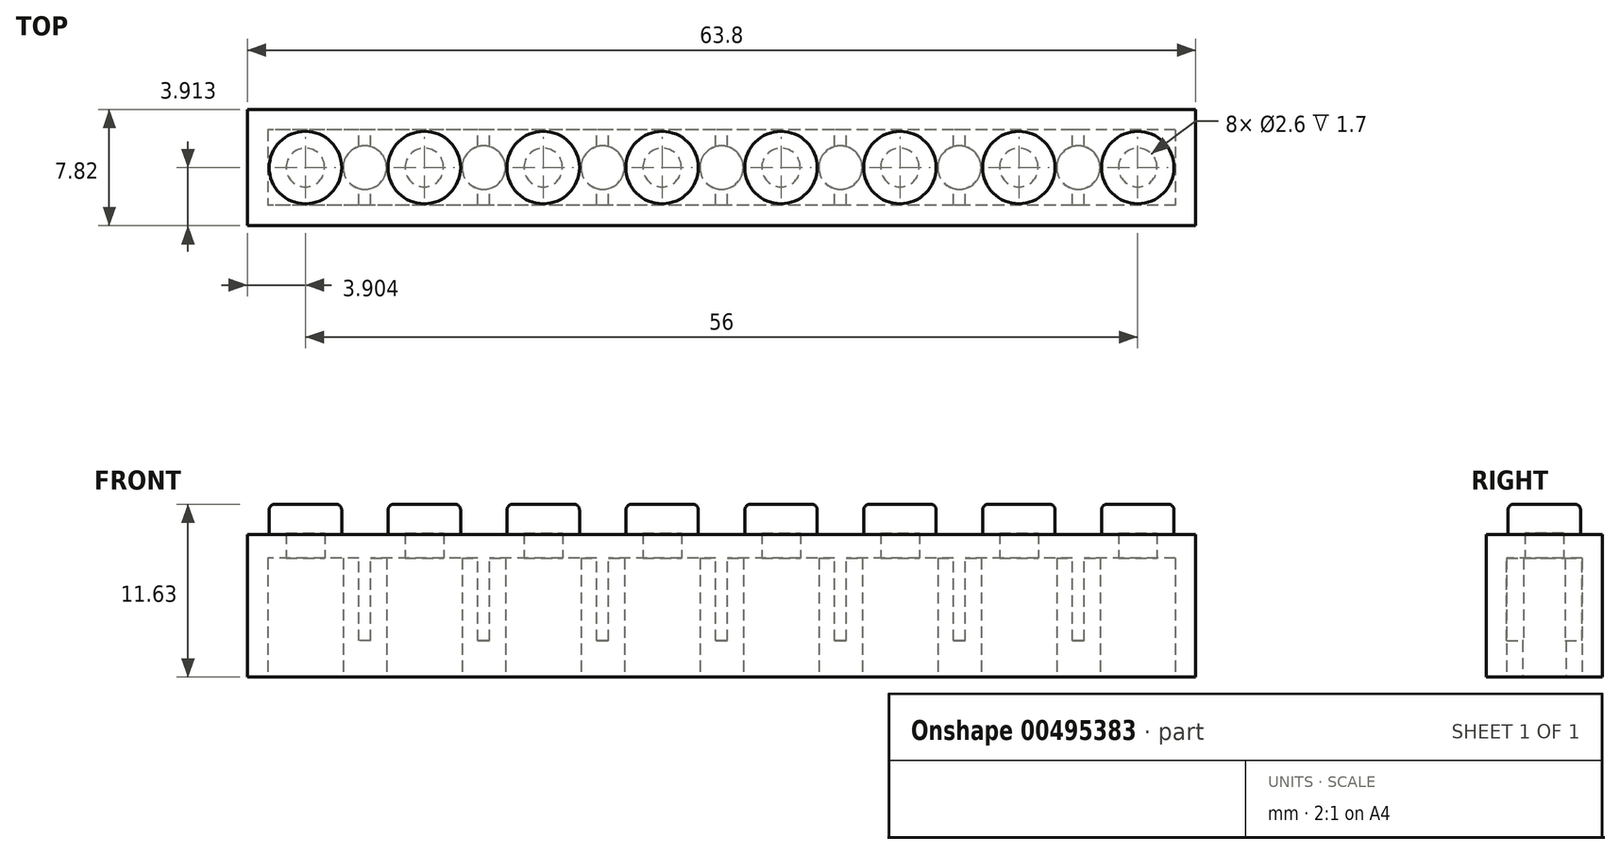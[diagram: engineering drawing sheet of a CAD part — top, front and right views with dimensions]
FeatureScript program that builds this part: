
annotation { "Feature Type Name" : "Feature", "Feature Type Description" : "" }
export const myFeature = defineFeature(function(context is Context, id is Id, definition is map)
    precondition{}
    {
        {
            var Q0;
            Q0=qCreatedBy(makeId("Top.planeOp"),FACE);
            var sketch = newSketch(context, id + "F0", { "sketchPlane" : qUnion([Q0])});
            skLineSegment(sketch, "E0.bottom", {"start": v(-34.24, -11.37) * mm, "end": v(29.56, -11.37) * mm});
            skLineSegment(sketch, "E0.top", {"start": v(-34.24, -19.19) * mm, "end": v(29.56, -19.19) * mm});
            skLineSegment(sketch, "E0.left", {"start": v(-34.24, -11.37) * mm, "end": v(-34.24, -19.19) * mm});
            skLineSegment(sketch, "E0.right", {"start": v(29.56, -11.37) * mm, "end": v(29.56, -19.19) * mm});
            skSolve(sketch);
        }
        {
            var Q0;
            Q0=qSketchRegion(id+"F0",true);
            extrude(context, id + "F1", {"entities" : qUnion([Q0]), "depth" : 9.6 * mm});
        }
        {
            var Q0;
            Q0=makeQuery(id+"F1.opExtrude","CAP_FACE",FACE,{"disambiguationData":[OSD([sQuery(id+"F0.wireOp",EDGE,"E0.bottom"),sQuery(id+"F0.wireOp",EDGE,"E0.top"),sQuery(id+"F0.wireOp",EDGE,"E0.left"),sQuery(id+"F0.wireOp",EDGE,"E0.right")])],"isStart":false});
            var sketch = newSketch(context, id + "F2", { "sketchPlane" : qUnion([Q0])});
            skCircle(sketch, "E1", {"center": v(-30.34, -15.28) * mm, "radius": 2.44 * mm});
            skLineSegment(sketch, "E2", {"start": v(-34.24, -15.28) * mm, "end": v(29.56, -15.28) * mm, "construction": true});
            skLineSegment(sketch, "E3", {"start": v(-2.34, -11.37) * mm, "end": v(-2.34, -19.19) * mm, "construction": true});
            skCircle(sketch, "E4.1.0.0", {"center": v(-22.34, -15.28) * mm, "radius": 2.44 * mm});
            skCircle(sketch, "E4.2.0.0", {"center": v(-14.34, -15.28) * mm, "radius": 2.44 * mm});
            skCircle(sketch, "E4.3.0.0", {"center": v(-6.34, -15.28) * mm, "radius": 2.44 * mm});
            skCircle(sketch, "E4.4.0.0", {"center": v(1.66, -15.28) * mm, "radius": 2.44 * mm});
            skCircle(sketch, "E4.5.0.0", {"center": v(9.66, -15.28) * mm, "radius": 2.44 * mm});
            skCircle(sketch, "E4.6.0.0", {"center": v(17.66, -15.28) * mm, "radius": 2.44 * mm});
            skCircle(sketch, "E4.7.0.0", {"center": v(25.66, -15.28) * mm, "radius": 2.44 * mm});
            skLineSegment(sketch, "E4.direction1", {"start": v(-30.34, -15.28) * mm, "end": v(-22.34, -15.28) * mm, "construction": true});
            skSolve(sketch);
        }
        {
            var Q0;
            Q0=qSketchRegion(id+"F2",true);
            extrude(context, id + "F3", {"entities" : qUnion([Q0]), "operationType" : NewBodyOperationType.ADD, "depth" : 2.03 * mm});
        }
        {
            var Q0;
            Q0=makeQuery(id+"F1.opExtrude","CAP_FACE",FACE,{"disambiguationData":[OSD([sQuery(id+"F0.wireOp",EDGE,"E0.bottom"),sQuery(id+"F0.wireOp",EDGE,"E0.top"),sQuery(id+"F0.wireOp",EDGE,"E0.left"),sQuery(id+"F0.wireOp",EDGE,"E0.right")])],"isStart":true});
            var sketch = newSketch(context, id + "F4", { "sketchPlane" : qUnion([Q0])});
            skLineSegment(sketch, "E5.bottom", {"start": v(28.2, 12.74) * mm, "end": v(-32.86, 12.74) * mm});
            skLineSegment(sketch, "E5.top", {"start": v(28.2, 17.82) * mm, "end": v(-32.86, 17.82) * mm});
            skLineSegment(sketch, "E5.left", {"start": v(28.2, 12.74) * mm, "end": v(28.2, 17.82) * mm});
            skLineSegment(sketch, "E5.right", {"start": v(-32.86, 12.74) * mm, "end": v(-32.86, 17.82) * mm});
            skLineSegment(sketch, "E6", {"start": v(-34.24, 15.28) * mm, "end": v(29.56, 15.28) * mm, "construction": true});
            skLineSegment(sketch, "E7", {"start": v(-2.34, 19.19) * mm, "end": v(-2.34, 11.37) * mm, "construction": true});
            skCircle(sketch, "E8", {"center": v(-26.34, 15.28) * mm, "radius": 1.46 * mm});
            skCircle(sketch, "E9.1.0.0", {"center": v(-18.34, 15.28) * mm, "radius": 1.46 * mm});
            skLineSegment(sketch, "E9.1.0.1", {"start": v(-26.24, 15.28) * mm, "end": v(37.56, 15.28) * mm, "construction": true});
            skCircle(sketch, "E9.2.0.0", {"center": v(-10.34, 15.28) * mm, "radius": 1.46 * mm});
            skLineSegment(sketch, "E9.2.0.1", {"start": v(-18.24, 15.28) * mm, "end": v(45.56, 15.28) * mm, "construction": true});
            skLineSegment(sketch, "E9.direction1", {"start": v(-26.34, 15.28) * mm, "end": v(-18.34, 15.28) * mm, "construction": true});
            skCircle(sketch, "E10.0.3.0", {"center": v(-2.34, 15.28) * mm, "radius": 1.46 * mm});
            skLineSegment(sketch, "E10.2.3.0", {"start": v(-10.24, 15.28) * mm, "end": v(53.56, 15.28) * mm, "construction": true});
            skCircle(sketch, "E10.0.4.0", {"center": v(5.66, 15.28) * mm, "radius": 1.46 * mm});
            skLineSegment(sketch, "E10.2.4.0", {"start": v(-2.24, 15.28) * mm, "end": v(61.56, 15.28) * mm, "construction": true});
            skCircle(sketch, "E10.0.5.0", {"center": v(13.66, 15.28) * mm, "radius": 1.46 * mm});
            skLineSegment(sketch, "E10.2.5.0", {"start": v(5.76, 15.28) * mm, "end": v(69.56, 15.28) * mm, "construction": true});
            skCircle(sketch, "E10.0.6.0", {"center": v(21.66, 15.28) * mm, "radius": 1.46 * mm});
            skLineSegment(sketch, "E10.2.6.0", {"start": v(13.76, 15.28) * mm, "end": v(77.56, 15.28) * mm, "construction": true});
            skSolve(sketch);
        }
        {
            var Q0;
            Q0=qSketchRegion(id+"F4",true);
            extrude(context, id + "F5", {"entities" : qUnion([Q0]), "operationType" : NewBodyOperationType.REMOVE, "oppositeDirection" : true, "depth" : (9.6 - 1.6) * mm});
        }
        {
            var Q0;
            Q0=makeQuery(id+"F3.opExtrude","CAP_EDGE",EDGE,{"disambiguationData":[OSD([sQuery(id+"F2.wireOp",EDGE,"E4.1.0.0")])],"isStart":false});
            var Q1;
            Q1=makeQuery(id+"F3.opExtrude","CAP_EDGE",EDGE,{"disambiguationData":[OSD([sQuery(id+"F2.wireOp",EDGE,"E4.2.0.0")])],"isStart":false});
            var Q2;
            Q2=makeQuery(id+"F3.opExtrude","CAP_EDGE",EDGE,{"disambiguationData":[OSD([sQuery(id+"F2.wireOp",EDGE,"E4.3.0.0")])],"isStart":false});
            var Q3;
            Q3=makeQuery(id+"F3.opExtrude","CAP_EDGE",EDGE,{"disambiguationData":[OSD([sQuery(id+"F2.wireOp",EDGE,"E4.4.0.0")])],"isStart":false});
            var Q4;
            Q4=makeQuery(id+"F3.opExtrude","CAP_EDGE",EDGE,{"disambiguationData":[OSD([sQuery(id+"F2.wireOp",EDGE,"E4.5.0.0")])],"isStart":false});
            var Q5;
            Q5=makeQuery(id+"F3.opExtrude","CAP_EDGE",EDGE,{"disambiguationData":[OSD([sQuery(id+"F2.wireOp",EDGE,"E4.6.0.0")])],"isStart":false});
            var Q6;
            Q6=makeQuery(id+"F3.opExtrude","CAP_EDGE",EDGE,{"disambiguationData":[OSD([sQuery(id+"F2.wireOp",EDGE,"E4.7.0.0")])],"isStart":false});
            var Q7;
            Q7=makeQuery(id+"F3.opExtrude","CAP_EDGE",EDGE,{"disambiguationData":[OSD([sQuery(id+"F2.wireOp",EDGE,"E1")])],"isStart":false});
            fillet(context, id + "F6", {"entities" : qUnion([Q0, Q1, Q2, Q3, Q4, Q5, Q6, Q7]), "radius" : 0.38 * mm, "tangentPropagation" : true, "allowEdgeOverflow" : false});
        }
        {
            var Q0;
            Q0=makeQuery(id+"F5.boolean.opBoolean","COPY",FACE,{"derivedFrom":makeQuery(id+"F5.opExtrude","CAP_FACE",FACE,{"disambiguationData":[OSD([sQuery(id+"F4.wireOp",EDGE,"E5.bottom"),sQuery(id+"F4.wireOp",EDGE,"E5.top"),sQuery(id+"F4.wireOp",EDGE,"E5.left"),sQuery(id+"F4.wireOp",EDGE,"E5.right"),sQuery(id+"F4.wireOp",EDGE,"E8"),sQuery(id+"F4.wireOp",EDGE,"E9.1.0.0"),sQuery(id+"F4.wireOp",EDGE,"E9.2.0.0"),sQuery(id+"F4.wireOp",EDGE,"E10.0.3.0"),sQuery(id+"F4.wireOp",EDGE,"E10.0.4.0"),sQuery(id+"F4.wireOp",EDGE,"E10.0.5.0"),sQuery(id+"F4.wireOp",EDGE,"E10.0.6.0")])],"isStart":false})});
            var sketch = newSketch(context, id + "F7", { "sketchPlane" : qUnion([Q0])});
            skLineSegment(sketch, "E11.bottom", {"start": v(-26.74, 17.82) * mm, "end": v(-25.94, 17.82) * mm});
            skLineSegment(sketch, "E11.top", {"start": v(-26.74, 12.74) * mm, "end": v(-25.94, 12.74) * mm});
            skLineSegment(sketch, "E11.left", {"start": v(-26.74, 17.82) * mm, "end": v(-26.74, 12.74) * mm});
            skLineSegment(sketch, "E11.right", {"start": v(-25.94, 17.82) * mm, "end": v(-25.94, 12.74) * mm});
            skPoint(sketch, "E11.middle", {"position": v(-26.34, 15.28) * mm});
            skLineSegment(sketch, "E12.1.0.0", {"start": v(-18.74, 17.82) * mm, "end": v(-17.94, 17.82) * mm});
            skLineSegment(sketch, "E12.1.0.1", {"start": v(-18.74, 17.82) * mm, "end": v(-18.74, 12.74) * mm});
            skLineSegment(sketch, "E12.1.0.2", {"start": v(-18.74, 12.74) * mm, "end": v(-17.94, 12.74) * mm});
            skLineSegment(sketch, "E12.1.0.3", {"start": v(-17.94, 17.82) * mm, "end": v(-17.94, 12.74) * mm});
            skLineSegment(sketch, "E12.2.0.0", {"start": v(-10.74, 17.82) * mm, "end": v(-9.94, 17.82) * mm});
            skLineSegment(sketch, "E12.2.0.1", {"start": v(-10.74, 17.82) * mm, "end": v(-10.74, 12.74) * mm});
            skLineSegment(sketch, "E12.2.0.2", {"start": v(-10.74, 12.74) * mm, "end": v(-9.94, 12.74) * mm});
            skLineSegment(sketch, "E12.2.0.3", {"start": v(-9.94, 17.82) * mm, "end": v(-9.94, 12.74) * mm});
            skLineSegment(sketch, "E12.3.0.0", {"start": v(-2.74, 17.82) * mm, "end": v(-1.94, 17.82) * mm});
            skLineSegment(sketch, "E12.3.0.1", {"start": v(-2.74, 17.82) * mm, "end": v(-2.74, 12.74) * mm});
            skLineSegment(sketch, "E12.3.0.2", {"start": v(-2.74, 12.74) * mm, "end": v(-1.94, 12.74) * mm});
            skLineSegment(sketch, "E12.3.0.3", {"start": v(-1.94, 17.82) * mm, "end": v(-1.94, 12.74) * mm});
            skLineSegment(sketch, "E12.4.0.0", {"start": v(5.26, 17.82) * mm, "end": v(6.06, 17.82) * mm});
            skLineSegment(sketch, "E12.4.0.1", {"start": v(5.26, 17.82) * mm, "end": v(5.26, 12.74) * mm});
            skLineSegment(sketch, "E12.4.0.2", {"start": v(5.26, 12.74) * mm, "end": v(6.06, 12.74) * mm});
            skLineSegment(sketch, "E12.4.0.3", {"start": v(6.06, 17.82) * mm, "end": v(6.06, 12.74) * mm});
            skLineSegment(sketch, "E12.5.0.0", {"start": v(13.26, 17.82) * mm, "end": v(14.06, 17.82) * mm});
            skLineSegment(sketch, "E12.5.0.1", {"start": v(13.26, 17.82) * mm, "end": v(13.26, 12.74) * mm});
            skLineSegment(sketch, "E12.5.0.2", {"start": v(13.26, 12.74) * mm, "end": v(14.06, 12.74) * mm});
            skLineSegment(sketch, "E12.5.0.3", {"start": v(14.06, 17.82) * mm, "end": v(14.06, 12.74) * mm});
            skLineSegment(sketch, "E12.6.0.0", {"start": v(21.26, 17.82) * mm, "end": v(22.06, 17.82) * mm});
            skLineSegment(sketch, "E12.6.0.1", {"start": v(21.26, 17.82) * mm, "end": v(21.26, 12.74) * mm});
            skLineSegment(sketch, "E12.6.0.2", {"start": v(21.26, 12.74) * mm, "end": v(22.06, 12.74) * mm});
            skLineSegment(sketch, "E12.6.0.3", {"start": v(22.06, 17.82) * mm, "end": v(22.06, 12.74) * mm});
            skLineSegment(sketch, "E12.direction1", {"start": v(-26.74, 12.74) * mm, "end": v(-18.74, 12.74) * mm, "construction": true});
            skSolve(sketch);
        }
        {
            var Q0;
            Q0=qSketchRegion(id+"F7",true);
            extrude(context, id + "F8", {"entities" : qUnion([Q0]), "operationType" : NewBodyOperationType.ADD, "depth" : 8 * mm - 2.44 * mm});
        }
        {
            var Q0;
            {var subQ0=sQuery(id+"F4.wireOp",EDGE,"E5.right");var subQ1=sQuery(id+"F4.wireOp",EDGE,"E5.top");var subQ2=sQuery(id+"F4.wireOp",EDGE,"E8");var subQ3=sQuery(id+"F4.wireOp",EDGE,"E5.bottom");var subQ4=sQuery(id+"F4.wireOp",EDGE,"E9.1.0.0");Q0=makeQuery(id+"F8.boolean.opBoolean","SPLIT",FACE,{"disambiguationData":[TD([makeQuery(id+"F5.boolean.opBoolean","COPY",FACE,{"derivedFrom":makeQuery(id+"F5.opExtrude","SWEPT_FACE",FACE,{"disambiguationData":[OSD([subQ0])]})})])],"derivedFrom":makeQuery(id+"F5.boolean.opBoolean","COPY",FACE,{"derivedFrom":makeQuery(id+"F5.opExtrude","CAP_FACE",FACE,{"disambiguationData":[OSD([subQ3,subQ1,sQuery(id+"F4.wireOp",EDGE,"E5.left"),subQ0,subQ2,subQ4,sQuery(id+"F4.wireOp",EDGE,"E9.2.0.0"),sQuery(id+"F4.wireOp",EDGE,"E10.0.3.0"),sQuery(id+"F4.wireOp",EDGE,"E10.0.4.0"),sQuery(id+"F4.wireOp",EDGE,"E10.0.5.0"),sQuery(id+"F4.wireOp",EDGE,"E10.0.6.0")])],"isStart":false})})});}
            var sketch = newSketch(context, id + "F9", { "sketchPlane" : qUnion([Q0])});
            skCircle(sketch, "E13", {"center": v(-30.34, 15.28) * mm, "radius": 1.3 * mm});
            skCircle(sketch, "E14.1.0.0", {"center": v(-22.34, 15.28) * mm, "radius": 1.3 * mm});
            skCircle(sketch, "E14.2.0.0", {"center": v(-14.34, 15.28) * mm, "radius": 1.3 * mm});
            skCircle(sketch, "E14.3.0.0", {"center": v(-6.34, 15.28) * mm, "radius": 1.3 * mm});
            skCircle(sketch, "E14.4.0.0", {"center": v(1.66, 15.28) * mm, "radius": 1.3 * mm});
            skCircle(sketch, "E14.5.0.0", {"center": v(9.66, 15.28) * mm, "radius": 1.3 * mm});
            skCircle(sketch, "E14.6.0.0", {"center": v(17.66, 15.28) * mm, "radius": 1.3 * mm});
            skLineSegment(sketch, "E14.direction1", {"start": v(-30.34, 15.28) * mm, "end": v(-22.34, 15.28) * mm, "construction": true});
            skCircle(sketch, "E15.0.7.0", {"center": v(25.66, 15.28) * mm, "radius": 1.3 * mm});
            skSolve(sketch);
        }
        {
            var Q0;
            Q0=qSketchRegion(id+"F9",true);
            extrude(context, id + "F10", {"entities" : qUnion([Q0]), "operationType" : NewBodyOperationType.REMOVE, "oppositeDirection" : true, "depth" : 1.7 * mm});
        }
    });
